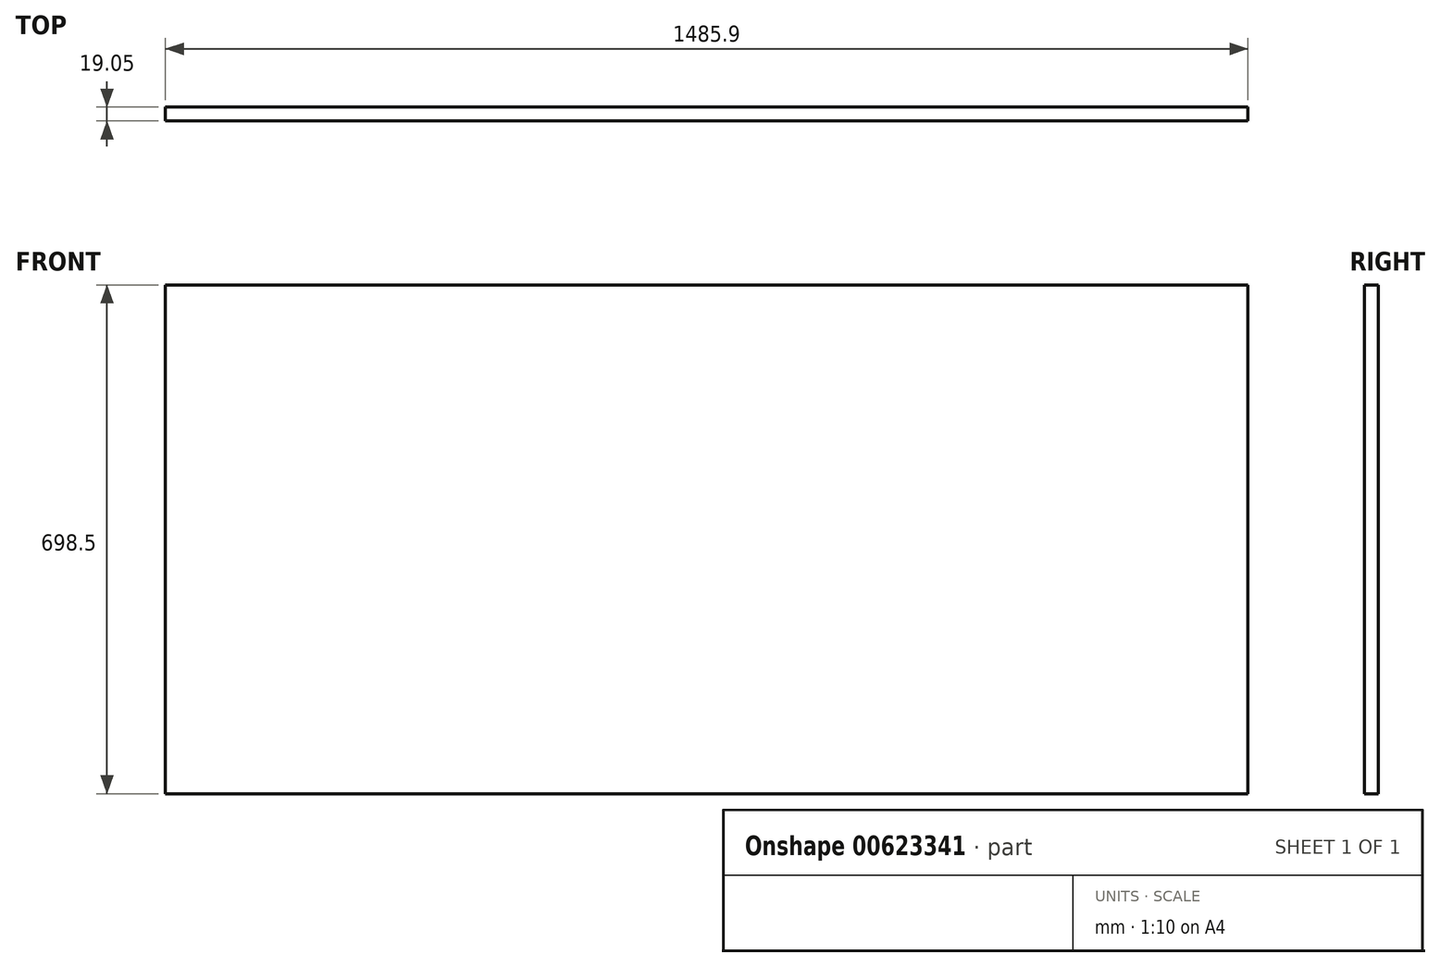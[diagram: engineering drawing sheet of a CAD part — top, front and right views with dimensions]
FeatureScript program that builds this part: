
annotation { "Feature Type Name" : "Feature", "Feature Type Description" : "" }
export const myFeature = defineFeature(function(context is Context, id is Id, definition is map)
    precondition{}
    {
        {
            var Q0;
            Q0=qCreatedBy(makeId("Front.planeOp"),FACE);
            var sketch = newSketch(context, id + "F0", { "sketchPlane" : qUnion([Q0])});
            skLineSegment(sketch, "E0.bottom", {"start": v(-742.95, 349.25) * mm, "end": v(742.95, 349.25) * mm});
            skLineSegment(sketch, "E0.top", {"start": v(-742.95, -349.25) * mm, "end": v(742.95, -349.25) * mm});
            skLineSegment(sketch, "E0.left", {"start": v(-742.95, 349.25) * mm, "end": v(-742.95, -349.25) * mm});
            skLineSegment(sketch, "E0.right", {"start": v(742.95, 349.25) * mm, "end": v(742.95, -349.25) * mm});
            skPoint(sketch, "E0.middle", {"position": v(0, 0) * mm});
            skSolve(sketch);
        }
        {
            var Q0;
            Q0=makeQuery(id+"F0.imprint","IMPRINT",FACE,{"disambiguationData":[TD([[makeQuery(id+"F0.imprint","IMPRINT",EDGE,{"derivedFrom":sQuery(id+"F0.wireOp",EDGE,"E0.bottom")}),-1.0]])]});
            extrude(context, id + "F1", {"entities" : qUnion([Q0]), "depth" : 19.05 * mm, "offsetDistance" : 25.4 * mm});
        }
    });
